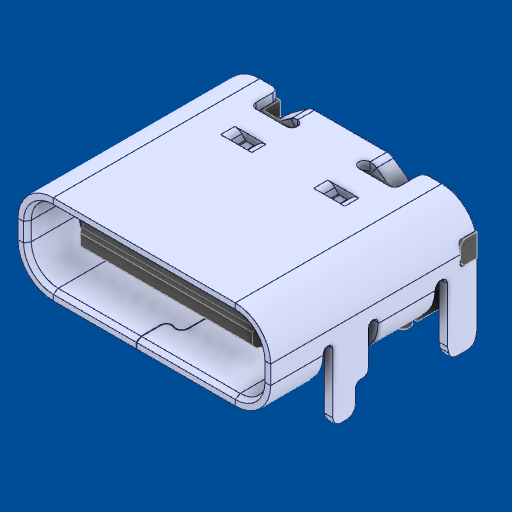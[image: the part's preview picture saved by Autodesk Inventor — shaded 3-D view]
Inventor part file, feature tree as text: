
AUTODESK INVENTOR PART (.ipt)
format: ipt  version: 2023.1 (Build 271208000, 208)  size: 646,656 bytes
history: native  units: in
note: dims shown in document units (in); Inventor stores cm internally (conversion verified against a paired STEP export)
features: other x33, mirror x8, boolean_combine x1
ambient origin geometry x8: Origin, YZ Plane, XZ Plane, XY Plane, X Axis, Y Axis, Z Axis, Center Point
bodies: Solid1 (feature_tree), Solid2 (feature_tree), Solid3 (feature_tree), Solid4 (feature_tree), Solid5 (feature_tree), Solid6 (feature_tree), Solid7 (feature_tree), Solid8 (feature_tree), Solid9 (feature_tree), Solid10 (feature_tree), Solid11 (feature_tree), Solid12 (feature_tree), Solid13 (feature_tree), Solid14 (feature_tree), Solid15 (feature_tree), Solid16 (feature_tree), Solid17 (feature_tree), Solid18 (feature_tree), Solid19 (feature_tree), Solid20 (feature_tree), Solid21 (feature_tree), Solid22 (feature_tree), Solid23 (feature_tree), Solid24 (feature_tree), Solid25 (feature_tree), Solid26 (feature_tree), Solid27 (feature_tree), Solid28 (feature_tree), Solid29 (feature_tree), Solid30 (feature_tree), Solid31 (feature_tree), Solid32 (feature_tree), Solid33 (feature_tree), Solid34 (feature_tree), Solid35 (feature_tree), Solid36 (feature_tree), Solid37 (feature_tree), Solid38 (feature_tree), Solid39 (feature_tree), Solid40 (feature_tree), Solid41 (feature_tree), Solid42 (feature_tree)
feature tree (42):
  other  "Body-Move_Copy1[19]"
  other  "Body-Move_Copy1[5]"
  other  "Body-Move_Copy1[11]"
  other  "Body-Move_Copy1[21]"
  other  "Body-Move_Copy1[25]"
  other  "Body-Move_Copy1[18]"
  other  "Body-Move_Copy1[9]"
  other  "Body-Move_Copy1[1]"
  other  "Body-Move_Copy1[2]"
  other  "Body-Move_Copy1[14]"
  other  "Body-Move_Copy1[23]"
  parser-record x1  (decoder bookkeeping rows leaked as tree rows — omitted from the tree; the rows remain in map.json)
  other  "Body-Move_Copy1[10]"
  other  "Body-Move_Copy1[16]"
  other  "Body-Move_Copy1[20]"
  other  "Body-Move_Copy1[17]"
  other  "NONE:1"
  other  "Body-Move_Copy1[24]"
  other  "Body-Move_Copy1[7]"
  other  "Body-Move_Copy1[15]"
  other  "Body-Move_Copy1[3]"
  other  "Body-Move_Copy1[8]"
  other  "Body-Move_Copy1[4]"
  other  "Body-Move_Copy1[13]"
  other  "Boss-Extrude5[1]"
  other  "Boss-Extrude5[2]"
  other  "Boss-Extrude5[3]"
  other  "Boss-Extrude5[4]"
  other  "Boss-Extrude5[5]"
  other  "Boss-Extrude5[6]"
  other  "Boss-Extrude5[7]"
  other  "Boss-Extrude5[8]"
  mirror  "Mirror3[3]"
  mirror  "Mirror3[4]"
  mirror  "Mirror3[5]"
  mirror  "Mirror3[6]"
  mirror  "Mirror3[7]"
  mirror  "Mirror3[8]"
  mirror  "Mirror3[9]"
  mirror  "Mirror3[10]"
  boolean_combine  "Combine2"
  other  "Cut-Extrude11"
